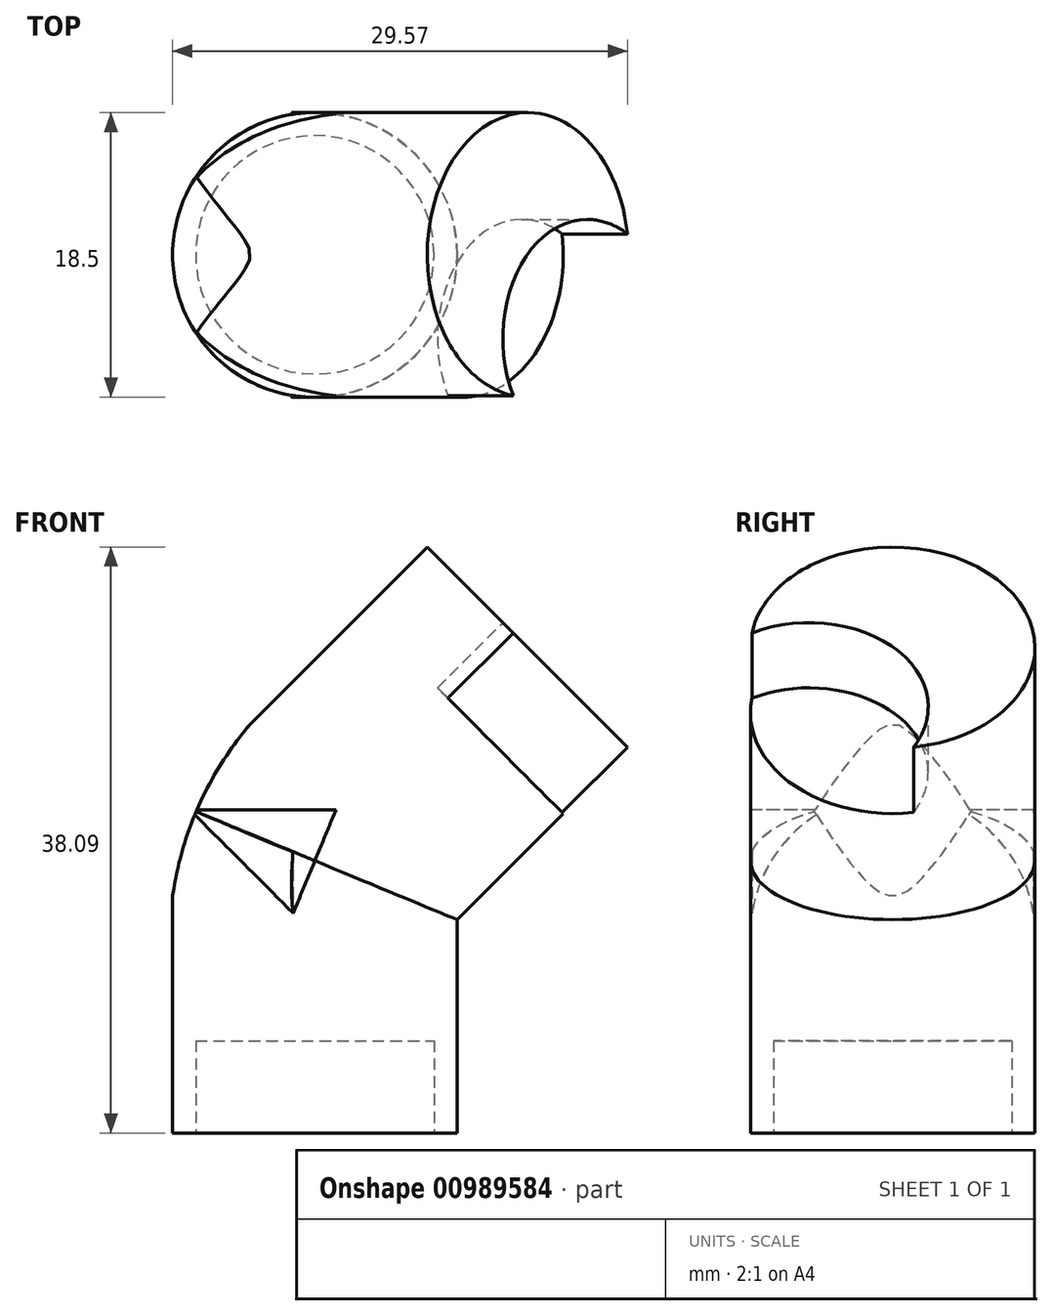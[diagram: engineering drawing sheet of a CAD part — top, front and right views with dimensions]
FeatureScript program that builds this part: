
annotation { "Feature Type Name" : "Feature", "Feature Type Description" : "" }
export const myFeature = defineFeature(function(context is Context, id is Id, definition is map)
    precondition{}
    {
        {
            var Q0;
            Q0=qCreatedBy(makeId("Front.planeOp"),FACE);
            var sketch = newSketch(context, id + "F0", { "sketchPlane" : qUnion([Q0])});
            skLineSegment(sketch, "E0", {"start": v(0.59, 8.29) * mm, "end": v(16.85, 24.55) * mm});
            skLineSegment(sketch, "E1", {"start": v(16.85, 24.55) * mm, "end": v(23.4, 18) * mm});
            skLineSegment(sketch, "E2", {"start": v(23.4, 18) * mm, "end": v(7.13, 1.75) * mm});
            skLineSegment(sketch, "E3", {"start": v(7.13, 1.75) * mm, "end": v(0.59, 8.29) * mm});
            skSolve(sketch);
        }
        {
            var Q0;
            Q0 = qSketchRegion(id + "F0", true);
            var Q1;
            Q1=sQuery(id+"F0.wireOp",EDGE,"E0");
            revolve(context, id + "F1", {"surfaceOperationType" : NewSurfaceOperationType.NEW, "entities" : qUnion([Q0]), "axis" : qUnion([Q1]), "revolveType" : RevolveType.FULL});
        }
        {
            var Q0;
            Q0=qCreatedBy(makeId("Front.planeOp"),FACE);
            var sketch = newSketch(context, id + "F2", { "sketchPlane" : qUnion([Q0])});
            skLineSegment(sketch, "E4.bottom", {"start": v(3, -7) * mm, "end": v(12.25, -7) * mm});
            skLineSegment(sketch, "E4.top", {"start": v(3, 14) * mm, "end": v(12.25, 14) * mm});
            skLineSegment(sketch, "E4.right", {"start": v(12.25, -7) * mm, "end": v(12.25, 14) * mm});
            skLineSegment(sketch, "E5", {"start": v(3, 14) * mm, "end": v(3, -7) * mm});
            skPoint(sketch, "E6.orphan", {"position": v(0, -7) * mm});
            skSolve(sketch);
        }
        {
            var Q0;
            Q0 = qSketchRegion(id + "F2", true);
            var Q1;
            Q1=sQuery(id+"F2.wireOp",EDGE,"E5");
            revolve(context, id + "F3", {"operationType" : NewBodyOperationType.ADD, "surfaceOperationType" : NewSurfaceOperationType.NEW, "entities" : qUnion([Q0]), "axis" : qUnion([Q1]), "revolveType" : RevolveType.FULL});
        }
        {
            var Q0;
            Q0=qCreatedBy(makeId("Front.planeOp"),FACE);
            var sketch = newSketch(context, id + "F4", { "sketchPlane" : qUnion([Q0])});
            skLineSegment(sketch, "E7", {"start": v(-6.3, 11.02) * mm, "end": v(-6.3, 16.04) * mm});
            skLineSegment(sketch, "E8", {"start": v(-6.3, 16.04) * mm, "end": v(0, 20.88) * mm});
            skLineSegment(sketch, "E9", {"start": v(-6.3, 11.02) * mm, "end": v(-6.3, 7.97) * mm});
            skArc(sketch, "E10", {"start": v(0, 20.88) * mm, "mid": v(-4.24, 14.95) * mm, "end": v(-6.3, 7.97) * mm});
            skSolve(sketch);
        }
        {
            var Q0;
            Q0 = qSketchRegion(id + "F4", true);
            extrude(context, id + "F5", {"entities" : qUnion([Q0]), "operationType" : NewBodyOperationType.REMOVE, "depth" : 25 * mm, "offsetDistance" : 25 * mm, "symmetric" : true});
        }
        {
            var Q0;
            Q0=makeQuery(id+"F3.opRevolve","SWEPT_FACE",FACE,{"disambiguationData":[OSD([sQuery(id+"F2.wireOp",EDGE,"E4.bottom")])]});
            var sketch = newSketch(context, id + "F6", { "sketchPlane" : qUnion([Q0])});
            skPoint(sketch, "E11", {"position": v(-4.8, 4.96) * mm});
            skPoint(sketch, "E12", {"position": v(1.58, 9.14) * mm});
            skArc(sketch, "E13", {"start": v(1.58, 9.14) * mm, "mid": v(-2.07, 7.75) * mm, "end": v(-4.8, 4.96) * mm});
            skArc(sketch, "E14", {"start": v(1.58, 9.14) * mm, "mid": v(-3.41, 9.8) * mm, "end": v(-4.8, 4.96) * mm});
            skArc(sketch, "E15.MirrorCS", {"start": v(1.58, -9.14) * mm, "mid": v(-2.07, -7.75) * mm, "end": v(-4.8, -4.96) * mm});
            skArc(sketch, "E16.MirrorCS", {"start": v(1.58, -9.14) * mm, "mid": v(-3.41, -9.8) * mm, "end": v(-4.8, -4.96) * mm});
            skSolve(sketch);
        }
        {
            var Q0;
            Q0 = qSketchRegion(id + "F6", true);
            extrude(context, id + "F7", {"entities" : qUnion([Q0]), "operationType" : NewBodyOperationType.REMOVE, "oppositeDirection" : true, "depth" : 30 * mm, "offsetDistance" : 25 * mm});
        }
        {
            var Q0;
            Q0=makeQuery(id+"F1.opRevolve","SWEPT_FACE",FACE,{"disambiguationData":[OSD([sQuery(id+"F0.wireOp",EDGE,"E1")])]});
            var sketch = newSketch(context, id + "F8", { "sketchPlane" : qUnion([Q0])});
            skCircle(sketch, "E17", {"center": v(-5.44, 0) * mm, "radius": 7.75 * mm});
            skSolve(sketch);
        }
        {
            var Q0;
            Q0 = qSketchRegion(id + "F8", true);
            extrude(context, id + "F9", {"entities" : qUnion([Q0]), "operationType" : NewBodyOperationType.REMOVE, "oppositeDirection" : true, "depth" : 6 * mm, "offsetDistance" : 25 * mm});
        }
        {
            var Q0;
            Q0=makeQuery(id+"F3.opRevolve","SWEPT_FACE",FACE,{"disambiguationData":[OSD([sQuery(id+"F2.wireOp",EDGE,"E4.bottom")])]});
            var sketch = newSketch(context, id + "F10", { "sketchPlane" : qUnion([Q0])});
            skCircle(sketch, "E18", {"center": v(3, 0) * mm, "radius": 7.75 * mm});
            skSolve(sketch);
        }
        {
            var Q0;
            Q0 = qSketchRegion(id + "F10", true);
            extrude(context, id + "F11", {"entities" : qUnion([Q0]), "operationType" : NewBodyOperationType.REMOVE, "oppositeDirection" : true, "depth" : 6 * mm, "offsetDistance" : 25 * mm});
        }
    });
